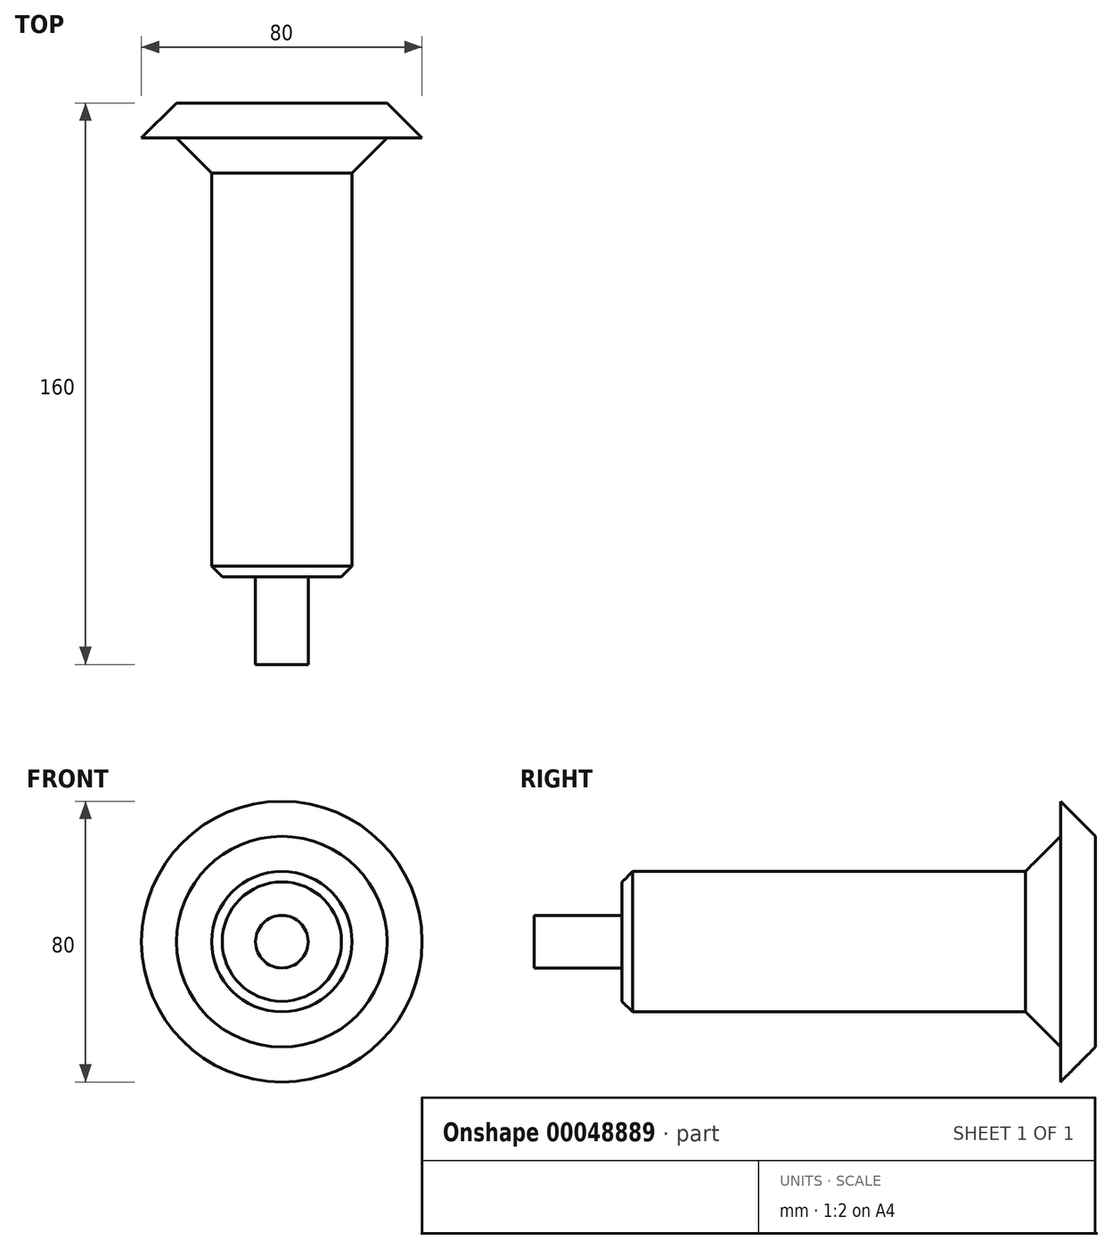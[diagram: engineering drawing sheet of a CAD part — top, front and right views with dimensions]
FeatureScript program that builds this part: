
annotation { "Feature Type Name" : "Feature", "Feature Type Description" : "" }
export const myFeature = defineFeature(function(context is Context, id is Id, definition is map)
    precondition{}
    {
        {
            var Q0;
            Q0=qCreatedBy(makeId("Right.planeOp"),FACE);
            var sketch = newSketch(context, id + "F0", { "sketchPlane" : qUnion([Q0])});
            skLineSegment(sketch, "E0", {"start": v(-65.6, 28.5) * mm, "end": v(-65.6, 36) * mm});
            skLineSegment(sketch, "E1", {"start": v(-65.6, 36) * mm, "end": v(-40.6, 36) * mm});
            skLineSegment(sketch, "E2", {"start": v(-40.6, 36) * mm, "end": v(-40.6, 48.5) * mm});
            skLineSegment(sketch, "E3", {"start": v(-40.6, 48.5) * mm, "end": v(84.4, 48.5) * mm});
            skLineSegment(sketch, "E4", {"start": v(84.4, 28.5) * mm, "end": v(-65.6, 28.5) * mm});
            skLineSegment(sketch, "E5", {"start": v(94.4, 68.5) * mm, "end": v(94.4, 28.5) * mm});
            skLineSegment(sketch, "E6", {"start": v(84.4, 48.5) * mm, "end": v(84.4, 68.5) * mm});
            skLineSegment(sketch, "E7", {"start": v(84.4, 68.5) * mm, "end": v(94.4, 68.5) * mm});
            skLineSegment(sketch, "E8", {"start": v(84.4, 28.5) * mm, "end": v(94.4, 28.5) * mm});
            skSolve(sketch);
        }
        {
            var Q0;
            Q0=makeQuery(id+"F0.imprint","IMPRINT",FACE,{"disambiguationData":[TD([[makeQuery(id+"F0.imprint","IMPRINT",EDGE,{"derivedFrom":sQuery(id+"F0.wireOp",EDGE,"E0")}),-1.0]])]});
            var Q1;
            Q1=sQuery(id+"F0.wireOp",EDGE,"E4");
            revolve(context, id + "F1", {"entities" : qUnion([Q0]), "axis" : qUnion([Q1]), "revolveType" : RevolveType.FULL});
        }
        {
            var Q0;
            Q0=makeQuery(id+"F1.opRevolve","SWEPT_EDGE",EDGE,{"disambiguationData":[OSD([sQuery(id+"F0.wireOp",EDGE,"E5"),sQuery(id+"F0.wireOp",EDGE,"E7")])]});
            chamfer(context, id + "F2", {"entities" : qUnion([Q0]), "chamferType" : ChamferType.OFFSET_ANGLE, "width" : 10 * mm, "oppositeDirection" : false, "angle" : 45 * degree, "tangentPropagation" : true});
        }
        {
            var Q0;
            Q0=makeQuery(id+"F1.opRevolve","SWEPT_EDGE",EDGE,{"disambiguationData":[OSD([sQuery(id+"F0.wireOp",EDGE,"E3"),sQuery(id+"F0.wireOp",EDGE,"E6")])]});
            chamfer(context, id + "F3", {"entities" : qUnion([Q0]), "chamferType" : ChamferType.OFFSET_ANGLE, "width" : 10 * mm, "oppositeDirection" : true, "angle" : 45 * degree, "tangentPropagation" : true});
        }
        {
            var Q0;
            Q0=makeQuery(id+"F1.opRevolve","SWEPT_EDGE",EDGE,{"disambiguationData":[OSD([sQuery(id+"F0.wireOp",EDGE,"E2"),sQuery(id+"F0.wireOp",EDGE,"E3")])]});
            chamfer(context, id + "F4", {"entities" : qUnion([Q0]), "chamferType" : ChamferType.OFFSET_ANGLE, "width" : 3 * mm, "oppositeDirection" : false, "angle" : 45 * degree, "tangentPropagation" : true});
        }
    });
